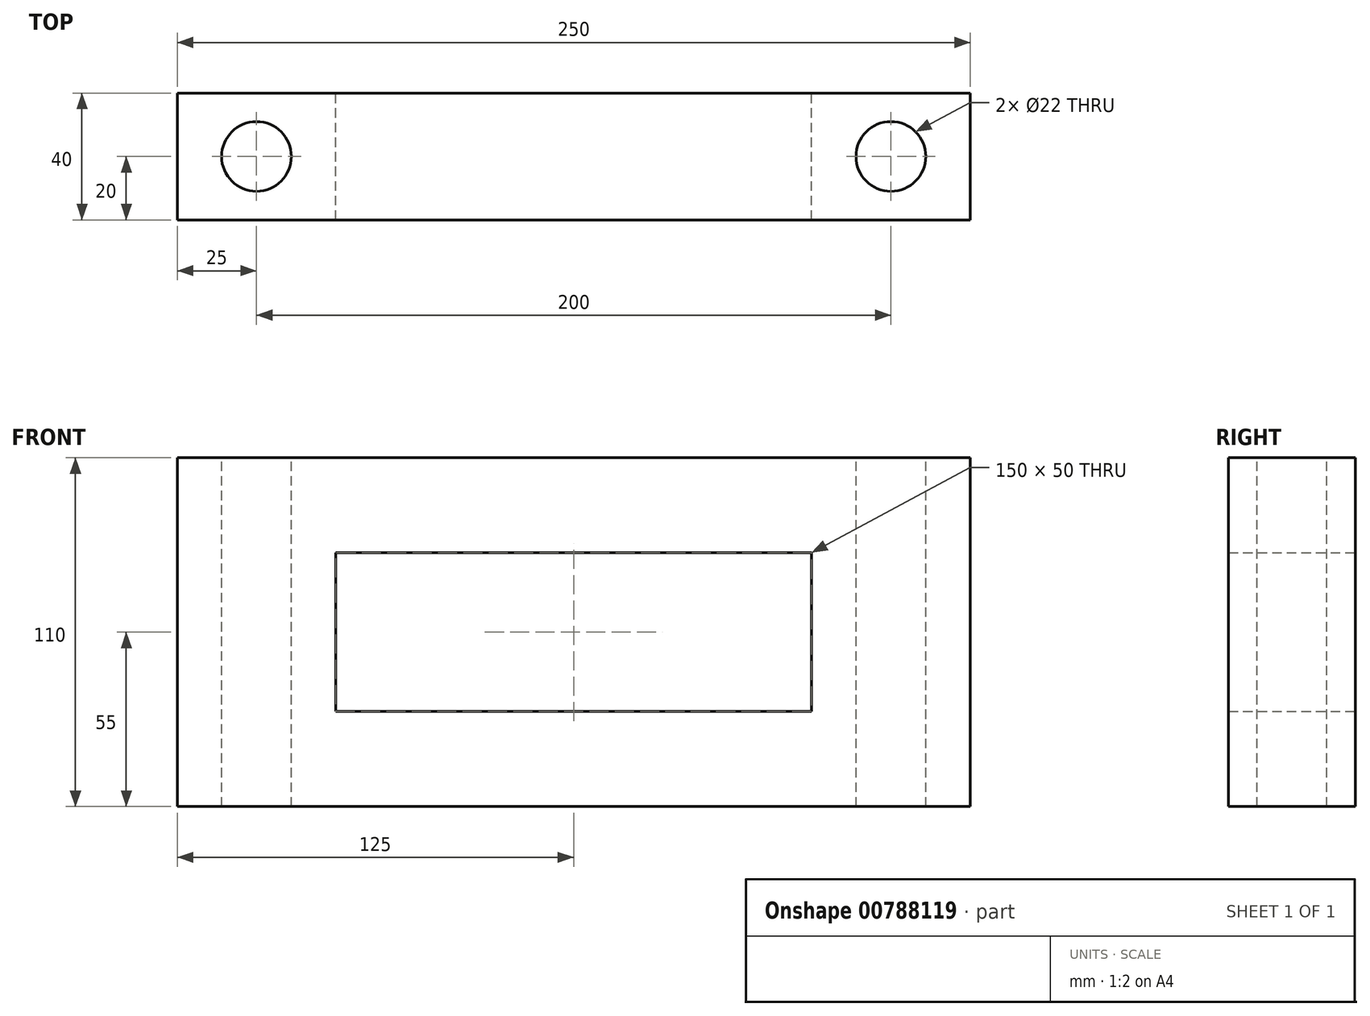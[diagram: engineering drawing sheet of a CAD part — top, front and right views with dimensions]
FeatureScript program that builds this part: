
annotation { "Feature Type Name" : "Feature", "Feature Type Description" : "" }
export const myFeature = defineFeature(function(context is Context, id is Id, definition is map)
    precondition{}
    {
        {
            var Q0;
            Q0=qCreatedBy(makeId("Front.planeOp"),FACE);
            var sketch = newSketch(context, id + "F0", { "sketchPlane" : qUnion([Q0])});
            skLineSegment(sketch, "E0.bottom", {"start": v(-75, -25) * mm, "end": v(75, -25) * mm});
            skLineSegment(sketch, "E0.top", {"start": v(-75, 25) * mm, "end": v(75, 25) * mm});
            skLineSegment(sketch, "E0.left", {"start": v(-75, -25) * mm, "end": v(-75, 25) * mm});
            skLineSegment(sketch, "E0.right", {"start": v(75, -25) * mm, "end": v(75, 25) * mm});
            skLineSegment(sketch, "E1.bottom", {"start": v(125, 55) * mm, "end": v(-125, 55) * mm});
            skLineSegment(sketch, "E1.top", {"start": v(125, -55) * mm, "end": v(-125, -55) * mm});
            skLineSegment(sketch, "E1.left", {"start": v(125, 55) * mm, "end": v(125, -55) * mm});
            skLineSegment(sketch, "E1.right", {"start": v(-125, 55) * mm, "end": v(-125, -55) * mm});
            skPoint(sketch, "E2", {"position": v(-75, 0) * mm});
            skPoint(sketch, "E3", {"position": v(0, -25) * mm});
            skPoint(sketch, "E4", {"position": v(0, -55) * mm});
            skPoint(sketch, "E5", {"position": v(-125, 0) * mm});
            skSolve(sketch);
        }
        {
            var Q0;
            Q0 = qSketchRegion(id + "F0", true);
            extrude(context, id + "F1", {"entities" : qUnion([Q0]), "depth" : 40 * mm, "offsetDistance" : 25 * mm});
        }
        {
            var Q0;
            Q0=makeQuery(id+"F1.opExtrude","SWEPT_FACE",FACE,{"disambiguationData":[OSD([sQuery(id+"F0.wireOp",EDGE,"E1.bottom")])]});
            var sketch = newSketch(context, id + "F2", { "sketchPlane" : qUnion([Q0])});
            skCircle(sketch, "E6", {"center": v(-100, -20) * mm, "radius": 11 * mm});
            skCircle(sketch, "E7", {"center": v(100, -20) * mm, "radius": 11 * mm});
            skPoint(sketch, "E8", {"position": v(-125, -20) * mm});
            skSolve(sketch);
        }
        {
            var Q0;
            Q0 = qSketchRegion(id + "F2", true);
            extrude(context, id + "F3", {"entities" : qUnion([Q0]), "operationType" : NewBodyOperationType.REMOVE, "oppositeDirection" : true, "depth" : 300 * mm, "offsetDistance" : 25 * mm});
        }
    });
